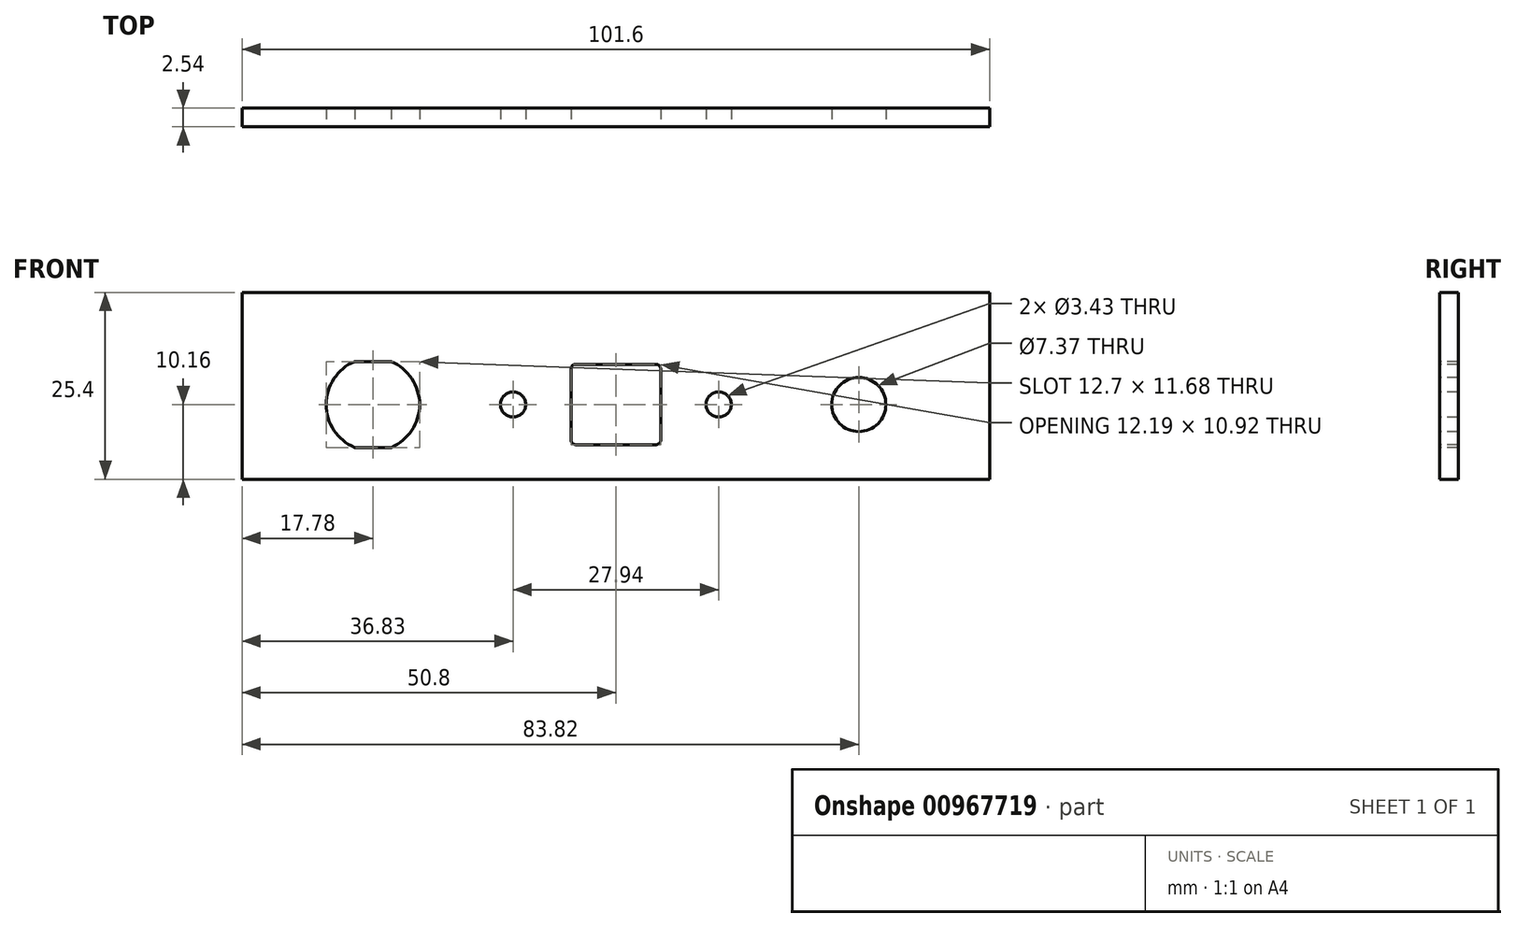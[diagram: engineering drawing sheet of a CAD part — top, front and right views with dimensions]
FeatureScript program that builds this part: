
annotation { "Feature Type Name" : "Feature", "Feature Type Description" : "" }
export const myFeature = defineFeature(function(context is Context, id is Id, definition is map)
    precondition{}
    {
        {
            var Q0;
            Q0=qCreatedBy(makeId("Front.planeOp"),FACE);
            var sketch = newSketch(context, id + "F0", { "sketchPlane" : qUnion([Q0])});
            skLineSegment(sketch, "E0.bottom", {"start": v(-50.8, 15.24) * mm, "end": v(50.8, 15.24) * mm});
            skLineSegment(sketch, "E0.top", {"start": v(-50.8, -10.16) * mm, "end": v(50.8, -10.16) * mm});
            skLineSegment(sketch, "E0.left", {"start": v(-50.8, 15.24) * mm, "end": v(-50.8, -10.16) * mm});
            skLineSegment(sketch, "E0.right", {"start": v(50.8, 15.24) * mm, "end": v(50.8, -10.16) * mm});
            skSolve(sketch);
        }
        {
            var Q0;
            Q0 = qSketchRegion(id + "F0", true);
            extrude(context, id + "F1", {"entities" : qUnion([Q0]), "oppositeDirection" : true, "depth" : 2.54 * mm, "offsetDistance" : 25.4 * mm});
        }
        {
            var Q0;
            Q0=makeQuery(id+"F1.opExtrude","CAP_FACE",FACE,{"disambiguationData":[OSD([sQuery(id+"F0.wireOp",EDGE,"E0.bottom"),sQuery(id+"F0.wireOp",EDGE,"E0.top"),sQuery(id+"F0.wireOp",EDGE,"E0.left"),sQuery(id+"F0.wireOp",EDGE,"E0.right")])],"isStart":true});
            var sketch = newSketch(context, id + "F2", { "sketchPlane" : qUnion([Q0])});
            skLineSegment(sketch, "E1", {"start": v(-89.54, 0) * mm, "end": v(100.58, 0) * mm, "construction": true});
            skLineSegment(sketch, "E2", {"start": v(-33.02, 13.33) * mm, "end": v(-33.02, -30.86) * mm, "construction": true});
            skArc(sketch, "E3", {"start": v(-35.5, 5.84) * mm, "mid": v(-39.37, 0) * mm, "end": v(-35.5, -5.84) * mm});
            skLineSegment(sketch, "E4.bottom", {"start": v(-30.53, 5.84) * mm, "end": v(-35.5, 5.84) * mm});
            skLineSegment(sketch, "E4.top", {"start": v(-30.53, -5.84) * mm, "end": v(-35.5, -5.84) * mm});
            skArc(sketch, "E5.trimOffspring", {"start": v(-30.53, -5.84) * mm, "mid": v(-26.67, 0) * mm, "end": v(-30.53, 5.84) * mm});
            skPoint(sketch, "E6.orphan", {"position": v(-42.28, 5.84) * mm});
            skPoint(sketch, "E7.orphan", {"position": v(-42.28, -5.84) * mm});
            skPoint(sketch, "E8.orphan", {"position": v(-23.76, -5.84) * mm});
            skPoint(sketch, "E4.left.start.orphan", {"position": v(-23.76, 5.84) * mm});
            skCircle(sketch, "E9", {"center": v(-13.97, 0) * mm, "radius": 1.71 * mm});
            skCircle(sketch, "E10.MirrorC", {"center": v(13.97, 0) * mm, "radius": 1.71 * mm});
            skLineSegment(sketch, "E11", {"start": v(33.02, 18.08) * mm, "end": v(33.02, -16.37) * mm, "construction": true});
            skCircle(sketch, "E12", {"center": v(33.02, 0) * mm, "radius": 3.68 * mm});
            skLineSegment(sketch, "E13.bottom", {"start": v(5.46, 5.46) * mm, "end": v(-5.46, 5.46) * mm});
            skLineSegment(sketch, "E13.top", {"start": v(5.46, -5.46) * mm, "end": v(-5.46, -5.46) * mm});
            skLineSegment(sketch, "E13.left", {"start": v(6.1, 4.83) * mm, "end": v(6.1, -4.83) * mm});
            skLineSegment(sketch, "E13.right", {"start": v(-6.1, 4.83) * mm, "end": v(-6.1, -4.83) * mm});
            skPoint(sketch, "E13.middle", {"position": v(0, 0) * mm});
            skPoint(sketch, "E14.visualSharp", {"position": v(-6.1, 5.46) * mm});
            skArc(sketch, "E14.filletArc", {"start": v(-5.46, 5.46) * mm, "mid": v(-5.91, 5.28) * mm, "end": v(-6.1, 4.83) * mm});
            skPoint(sketch, "E15.visualSharp", {"position": v(6.1, 5.46) * mm});
            skArc(sketch, "E15.filletArc", {"start": v(6.1, 4.83) * mm, "mid": v(5.91, 5.28) * mm, "end": v(5.46, 5.46) * mm});
            skPoint(sketch, "E16.visualSharp", {"position": v(6.1, -5.46) * mm});
            skArc(sketch, "E16.filletArc", {"start": v(5.46, -5.46) * mm, "mid": v(5.91, -5.28) * mm, "end": v(6.1, -4.83) * mm});
            skPoint(sketch, "E17.visualSharp", {"position": v(-6.1, -5.46) * mm});
            skArc(sketch, "E17.filletArc", {"start": v(-6.1, -4.83) * mm, "mid": v(-5.91, -5.28) * mm, "end": v(-5.46, -5.46) * mm});
            skSolve(sketch);
        }
        {
            var Q0;
            Q0 = qSketchRegion(id + "F2", true);
            extrude(context, id + "F3", {"entities" : qUnion([Q0]), "operationType" : NewBodyOperationType.REMOVE, "endBound" : BoundingType.THROUGH_ALL, "oppositeDirection" : true, "depth" : 25.4 * mm, "offsetDistance" : 25.4 * mm});
        }
    });
